annotation { "Feature Type Name" : "Feature", "Feature Type Description" : "" }
export const myFeature = defineFeature(function(context is Context, id is Id, definition is map)
    precondition{}
    {
        {
            var Q0;
            Q0=qCreatedBy(makeId("Top.planeOp"),FACE);
            var sketch = newSketch(context, id + "F0", { "sketchPlane" : qUnion([Q0])});
            skFitSpline(sketch, "E0", {"points": [v(-75.9, 56.3) * mm, v(-41.27, 55.73) * mm, v(0, 76.16) * mm], "startDerivative": vector(72, -44.5) * mm, "endDerivative": vector(80.7, 41.05) * mm});
            skFitSpline(sketch, "E1", {"points": [v(-75.9, 56.3) * mm, v(-55.54, -24.54) * mm, v(0, -75.8) * mm], "startDerivative": vector(4.41, -141.69) * mm, "endDerivative": vector(145.68, -108.7) * mm});
            skFitSpline(sketch, "E2.MirrorCS", {"points": [v(75.9, 56.3) * mm, v(41.27, 55.73) * mm, v(0, 76.16) * mm], "startDerivative": vector(-72, -44.5) * mm, "endDerivative": vector(-80.7, 41.05) * mm});
            skFitSpline(sketch, "E3.MirrorCS", {"points": [v(75.9, 56.3) * mm, v(55.54, -24.54) * mm, v(0, -75.8) * mm], "startDerivative": vector(-4.41, -141.69) * mm, "endDerivative": vector(-145.68, -108.7) * mm});
            skLineSegment(sketch, "E4", {"start": v(-68.95, 9.35) * mm, "end": v(68.95, 9.35) * mm});
            skLineSegment(sketch, "E5", {"start": v(0, 9.35) * mm, "end": v(-55.54, -24.54) * mm});
            skLineSegment(sketch, "E6", {"start": v(-46.2, -37.67) * mm, "end": v(0, -8.4) * mm});
            skLineSegment(sketch, "E7.MirrorCS", {"start": v(0, 9.35) * mm, "end": v(55.54, -24.54) * mm});
            skLineSegment(sketch, "E8.MirrorCS", {"start": v(46.2, -37.67) * mm, "end": v(0, -8.4) * mm});
            skLineSegment(sketch, "E9", {"start": v(-74, 34.57) * mm, "end": v(74, 34.57) * mm});
            skSolve(sketch);
        }
        {
            var Q0;
            {var subQ0=sQuery(id+"F0.wireOp",EDGE,"E4");Q0=makeQuery(id+"F0.imprint","IMPRINT",FACE,{"disambiguationData":[TD([[makeQuery(id+"F0.imprint","IMPRINT",EDGE,{"derivedFrom":subQ0}),1.0]])]});}
            extrude(context, id + "F1", {"entities" : qUnion([Q0]), "depth" : 25.4 * mm, "offsetDistance" : 25.4 * mm});
        }
        {
            var Q0;
            {var subQ1=sQuery(id+"F0.wireOp",EDGE,"E5");Q0=makeQuery(id+"F0.imprint","IMPRINT",FACE,{"disambiguationData":[TD([[makeQuery(id+"F0.imprint","IMPRINT",EDGE,{"derivedFrom":subQ1}),1.0]])]});}
            extrude(context, id + "F2", {"entities" : qUnion([Q0]), "operationType" : NewBodyOperationType.ADD, "depth" : 25.4 * mm, "offsetDistance" : 25.4 * mm});
        }
        {
            var Q0;
            {var subQ4=sQuery(id+"F0.wireOp",EDGE,"E0");Q0=makeQuery(id+"F0.imprint","IMPRINT",FACE,{"disambiguationData":[TD([[makeQuery(id+"F0.imprint","IMPRINT",EDGE,{"derivedFrom":subQ4}),-1.0]])]});}
            var Q1;
            {var subQ3=sQuery(id+"F0.wireOp",EDGE,"E5");Q1=makeQuery(id+"F0.imprint","IMPRINT",FACE,{"disambiguationData":[TD([[makeQuery(id+"F0.imprint","IMPRINT",EDGE,{"derivedFrom":subQ3}),-1.0]])]});}
            var Q2;
            {var subQ3=sQuery(id+"F0.wireOp",EDGE,"E7.MirrorCS");Q2=makeQuery(id+"F0.imprint","IMPRINT",FACE,{"disambiguationData":[TD([[makeQuery(id+"F0.imprint","IMPRINT",EDGE,{"derivedFrom":subQ3}),1.0]])]});}
            var Q3;
            {var subQ3=sQuery(id+"F0.wireOp",EDGE,"E6");Q3=makeQuery(id+"F0.imprint","IMPRINT",FACE,{"disambiguationData":[TD([[makeQuery(id+"F0.imprint","IMPRINT",EDGE,{"derivedFrom":subQ3}),-1.0]])]});}
            extrude(context, id + "F3", {"entities" : qUnion([Q0, Q1, Q2, Q3]), "depth" : 12.7 * mm, "offsetDistance" : 25.4 * mm});
        }
        {
            var Q0;
            Q0=makeQuery(id+"F1.opExtrude","CAP_FACE",FACE,{"disambiguationData":[OSD([sQuery(id+"F0.wireOp",EDGE,"E1"),sQuery(id+"F0.wireOp",EDGE,"E3.MirrorCS"),sQuery(id+"F0.wireOp",EDGE,"E4"),sQuery(id+"F0.wireOp",EDGE,"E9")])],"isStart":false});
            var sketch = newSketch(context, id + "F4", { "sketchPlane" : qUnion([Q0])});
            skText(sketch, "E10", { "text": "Alwin Mao", "fontName": "OpenSans-Bold.ttf"});
            const initialGuessF4  = {"E10": [-0.06989, 0.01304, 1, 0, 0.01914]};
            skSetInitialGuess(sketch, initialGuessF4);
            skSolve(sketch);
        }
        {
            var Q0;
            Q0 = qSketchRegion(id + "F4", true);
            extrude(context, id + "F5", {"entities" : qUnion([Q0]), "operationType" : NewBodyOperationType.ADD, "depth" : 2.54 * mm, "offsetDistance" : 25.4 * mm});
        }
    });